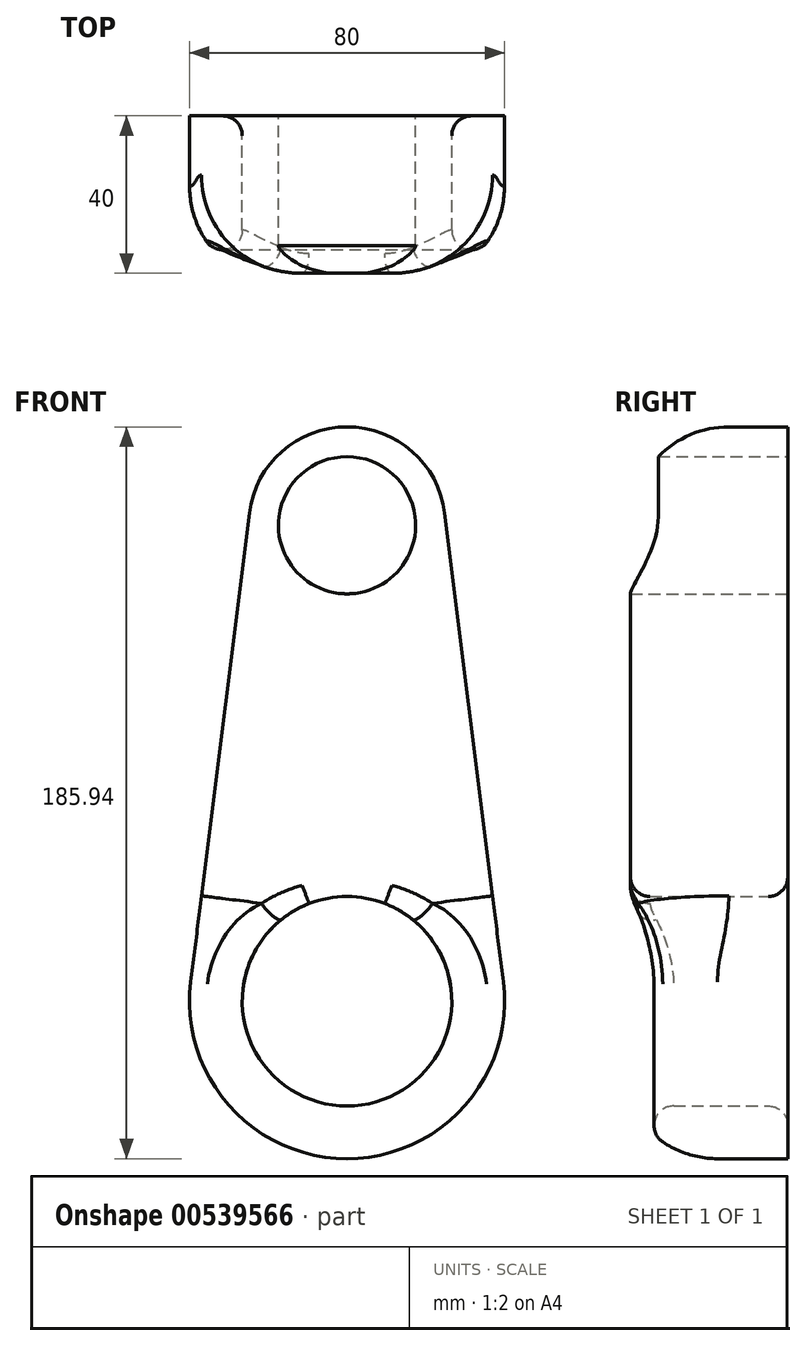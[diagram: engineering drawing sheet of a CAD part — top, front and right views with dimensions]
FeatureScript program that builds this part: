
annotation { "Feature Type Name" : "Feature", "Feature Type Description" : "" }
export const myFeature = defineFeature(function(context is Context, id is Id, definition is map)
    precondition{}
    {
        {
            var Q0;
            Q0=qCreatedBy(makeId("Front.planeOp"),FACE);
            var sketch = newSketch(context, id + "F0", { "sketchPlane" : qUnion([Q0])});
            skCircle(sketch, "E0", {"center": v(0, -20.27) * mm, "radius": 40 * mm});
            skCircle(sketch, "E1", {"center": v(0, 100.67) * mm, "radius": 25 * mm});
            skLineSegment(sketch, "E2", {"start": v(-24.8, 103.77) * mm, "end": v(-39.7, -15.3) * mm});
            skLineSegment(sketch, "E3", {"start": v(24.8, 103.77) * mm, "end": v(39.7, -15.3) * mm});
            skCircle(sketch, "E4", {"center": v(0, 100.67) * mm, "radius": 17.43 * mm});
            skCircle(sketch, "E5", {"center": v(0, -20.27) * mm, "radius": 26.62 * mm});
            skSolve(sketch);
        }
        {
            var Q0;
            Q0 = qSketchRegion(id + "F0", true);
            var sketch = newSketch(context, id + "F1", { "sketchPlane" : qUnion([Q0])});
            skSolve(sketch);
        }
        {
            var Q0;
            Q0=makeQuery(id+"F0.imprint","IMPRINT",FACE,{"disambiguationData":[TD([[makeQuery(id+"F0.imprint","IMPRINT",EDGE,{"derivedFrom":sQuery(id+"F0.wireOp",EDGE,"E5")}),-1.0]])]});
            var Q1;
            {var subQ0=sQuery(id+"F0.wireOp",EDGE,"E2");Q1=makeQuery(id+"F0.imprint","IMPRINT",FACE,{"disambiguationData":[TD([[makeQuery(id+"F0.imprint","IMPRINT",EDGE,{"derivedFrom":subQ0}),1.0]])]});}
            var Q2;
            Q2=makeQuery(id+"F0.imprint","IMPRINT",FACE,{"disambiguationData":[TD([[makeQuery(id+"F0.imprint","IMPRINT",EDGE,{"derivedFrom":sQuery(id+"F0.wireOp",EDGE,"E4")}),-1.0]])]});
            extrude(context, id + "F2", {"entities" : qUnion([Q0, Q1, Q2]), "depth" : 40 * mm, "offsetDistance" : 25 * mm});
        }
        {
            var Q0;
            Q0=makeQuery(id+"F2.opExtrude","SWEPT_FACE",FACE,{"disambiguationData":[OSD([sQuery(id+"F0.wireOp",EDGE,"E3")])]});
            var sketch = newSketch(context, id + "F3", { "sketchPlane" : qUnion([Q0])});
            skSolve(sketch);
        }
        {
            var Q0;
            Q0=makeQuery(id+"F2.opExtrude","CAP_EDGE",EDGE,{"disambiguationData":[OSD([sQuery(id+"F0.wireOp",EDGE,"E3")])],"isStart":false});
            var Q1;
            Q1=makeQuery(id+"F2.opExtrude","CAP_EDGE",EDGE,{"disambiguationData":[OSD([sQuery(id+"F0.wireOp",EDGE,"E0")])],"isStart":false});
            var Q2;
            Q2=makeQuery(id+"F2.opExtrude","CAP_EDGE",EDGE,{"disambiguationData":[OSD([sQuery(id+"F0.wireOp",EDGE,"E2")])],"isStart":false});
            var Q3;
            Q3=makeQuery(id+"F2.opExtrude","CAP_EDGE",EDGE,{"disambiguationData":[OSD([sQuery(id+"F0.wireOp",EDGE,"E1")])],"isStart":false});
            fillet(context, id + "F4", {"entities" : qUnion([Q0, Q1, Q2, Q3]), "radius" : 25 * mm, "tangentPropagation" : true, "allowEdgeOverflow" : false});
        }
        {
            var Q0;
            Q0=makeQuery(id+"F2.opExtrude","SWEPT_FACE",FACE,{"disambiguationData":[OSD([sQuery(id+"F0.wireOp",EDGE,"E5")])]});
            fillet(context, id + "F5", {"entities" : qUnion([Q0]), "radius" : 5 * mm, "tangentPropagation" : true, "allowEdgeOverflow" : false});
        }
    });
